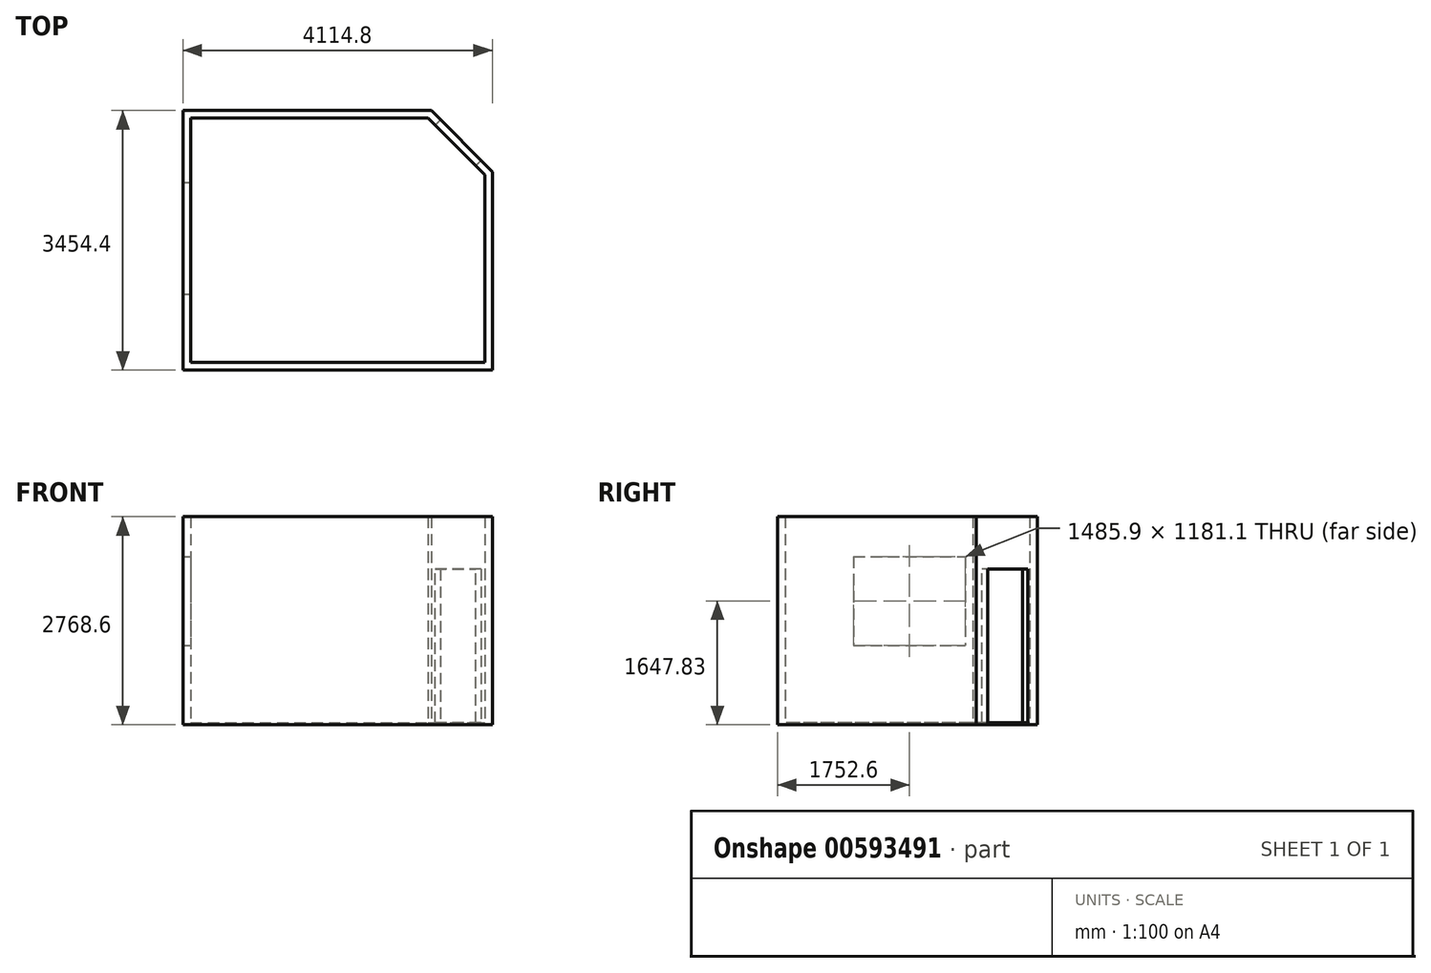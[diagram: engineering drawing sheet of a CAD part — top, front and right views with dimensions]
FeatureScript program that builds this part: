
annotation { "Feature Type Name" : "Feature", "Feature Type Description" : "" }
export const myFeature = defineFeature(function(context is Context, id is Id, definition is map)
    precondition{}
    {
        {
            var Q0;
            Q0=qCreatedBy(makeId("Top.planeOp"),FACE);
            var sketch = newSketch(context, id + "F0", { "sketchPlane" : qUnion([Q0])});
            skLineSegment(sketch, "E0.bottom", {"start": v(0, 0) * mm, "end": v(3157.26, 0) * mm});
            skLineSegment(sketch, "E0.top", {"start": v(0, -3251.2) * mm, "end": v(3911.6, -3251.2) * mm});
            skLineSegment(sketch, "E0.left", {"start": v(0, 0) * mm, "end": v(0, -3251.2) * mm});
            skLineSegment(sketch, "E0.right", {"start": v(3911.6, -754.34) * mm, "end": v(3911.6, -3251.2) * mm});
            skLineSegment(sketch, "E1", {"start": v(3157.26, 0) * mm, "end": v(3911.6, -754.34) * mm});
            skSolve(sketch);
        }
        {
            var Q0;
            Q0 = qSketchRegion(id + "F0", true);
            extrude(context, id + "F1", {"entities" : qUnion([Q0]), "oppositeDirection" : true, "depth" : 25.4 * mm, "offsetDistance" : 25.4 * mm});
        }
        {
            var Q0;
            Q0=qCreatedBy(makeId("Top.planeOp"),FACE);
            var sketch = newSketch(context, id + "F2", { "sketchPlane" : qUnion([Q0])});
            skLineSegment(sketch, "E2.0", {"start": v(-101.6, 101.6) * mm, "end": v(3199.34, 101.6) * mm});
            skLineSegment(sketch, "E3.0", {"start": v(3199.34, 101.6) * mm, "end": v(4013.2, -712.26) * mm});
            skLineSegment(sketch, "E4.0", {"start": v(4013.2, -712.26) * mm, "end": v(4013.2, -3352.8) * mm});
            skLineSegment(sketch, "E5.0", {"start": v(-101.6, 101.6) * mm, "end": v(-101.6, -3352.8) * mm});
            skLineSegment(sketch, "E6.0", {"start": v(-101.6, -3352.8) * mm, "end": v(4013.2, -3352.8) * mm});
            skSolve(sketch);
        }
        {
            var Q0;
            Q0 = qSketchRegion(id + "F2", true);
            extrude(context, id + "F3", {"entities" : qUnion([Q0]), "operationType" : NewBodyOperationType.ADD, "depth" : 2743.2 * mm, "offsetDistance" : 25.4 * mm});
        }
        {
            var Q0;
            Q0 = qSketchRegion(id + "F2", true);
            var Q1;
            Q1=makeQuery(id+"F1.opExtrude","CAP_FACE",FACE,{"disambiguationData":[OSD([sQuery(id+"F0.wireOp",EDGE,"E0.bottom"),sQuery(id+"F0.wireOp",EDGE,"E0.top"),sQuery(id+"F0.wireOp",EDGE,"E0.left"),sQuery(id+"F0.wireOp",EDGE,"E0.right"),sQuery(id+"F0.wireOp",EDGE,"E1")])],"isStart":false});
            extrude(context, id + "F4", {"entities" : qUnion([Q0]), "operationType" : NewBodyOperationType.ADD, "endBound" : BoundingType.UP_TO_SURFACE, "oppositeDirection" : true, "depth" : 25.4 * mm, "endBoundEntityFace" : qUnion([Q1]), "offsetDistance" : 25.4 * mm});
        }
        {
            var Q0;
            Q0 = qSketchRegion(id + "F0", true);
            extrude(context, id + "F5", {"entities" : qUnion([Q0]), "operationType" : NewBodyOperationType.REMOVE, "endBound" : BoundingType.THROUGH_ALL, "depth" : 25.4 * mm, "offsetDistance" : 25.4 * mm});
        }
        {
            var Q0;
            Q0=makeQuery(id+"F5.boolean.opBoolean","COPY",FACE,{"derivedFrom":makeQuery(id+"F5.opExtrude","SWEPT_FACE",FACE,{"disambiguationData":[OSD([sQuery(id+"F0.wireOp",EDGE,"E0.left")])]})});
            var sketch = newSketch(context, id + "F6", { "sketchPlane" : qUnion([Q0])});
            skLineSegment(sketch, "E7.bottom", {"start": v(-2343.15, 2212.98) * mm, "end": v(-857.25, 2212.98) * mm});
            skLineSegment(sketch, "E7.top", {"start": v(-2343.15, 1031.87) * mm, "end": v(-857.25, 1031.88) * mm});
            skLineSegment(sketch, "E7.left", {"start": v(-2343.15, 2212.98) * mm, "end": v(-2343.15, 1031.87) * mm});
            skLineSegment(sketch, "E7.right", {"start": v(-857.25, 2212.98) * mm, "end": v(-857.25, 1031.88) * mm});
            skSolve(sketch);
        }
        {
            var Q0;
            Q0 = qSketchRegion(id + "F6", true);
            extrude(context, id + "F7", {"entities" : qUnion([Q0]), "operationType" : NewBodyOperationType.REMOVE, "endBound" : BoundingType.THROUGH_ALL, "oppositeDirection" : true, "depth" : 25.4 * mm, "offsetDistance" : 25.4 * mm});
        }
        {
            var Q0;
            Q0=makeQuery(id+"F5.boolean.opBoolean","COPY",FACE,{"derivedFrom":makeQuery(id+"F5.opExtrude","SWEPT_FACE",FACE,{"disambiguationData":[OSD([sQuery(id+"F0.wireOp",EDGE,"E1")])]})});
            var sketch = newSketch(context, id + "F8", { "sketchPlane" : qUnion([Q0])});
            skLineSegment(sketch, "E8.bottom", {"start": v(2365.87, 0) * mm, "end": v(3127.87, 0) * mm});
            skLineSegment(sketch, "E8.top", {"start": v(2365.87, 2044.7) * mm, "end": v(3127.87, 2044.7) * mm});
            skLineSegment(sketch, "E8.left", {"start": v(2365.87, 0) * mm, "end": v(2365.87, 2044.7) * mm});
            skLineSegment(sketch, "E8.right", {"start": v(3127.87, 0) * mm, "end": v(3127.87, 2044.7) * mm});
            skSolve(sketch);
        }
        {
            var Q0;
            Q0 = qSketchRegion(id + "F8", true);
            extrude(context, id + "F9", {"entities" : qUnion([Q0]), "operationType" : NewBodyOperationType.REMOVE, "endBound" : BoundingType.THROUGH_ALL, "oppositeDirection" : true, "depth" : 25.4 * mm, "offsetDistance" : 25.4 * mm});
        }
    });
